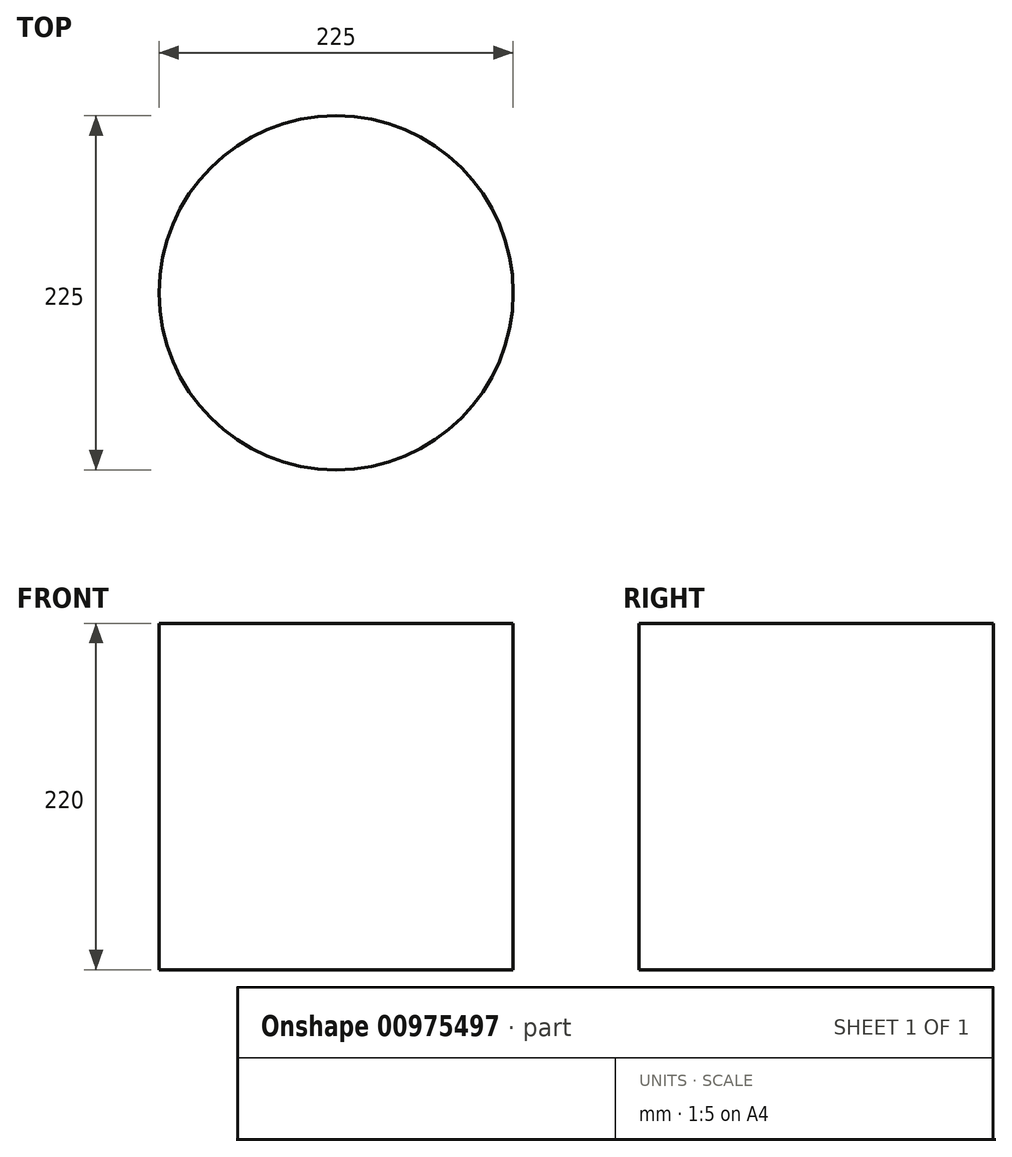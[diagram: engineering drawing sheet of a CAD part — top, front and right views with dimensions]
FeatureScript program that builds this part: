
annotation { "Feature Type Name" : "Feature", "Feature Type Description" : "" }
export const myFeature = defineFeature(function(context is Context, id is Id, definition is map)
    precondition{}
    {
        {
            var Q0;
            Q0=qCreatedBy(makeId("Top.planeOp"),FACE);
            var sketch = newSketch(context, id + "F0", { "sketchPlane" : qUnion([Q0])});
            skCircle(sketch, "E0", {"center": v(0, 0) * mm, "radius": 110.5 * mm});
            skSolve(sketch);
        }
        {
            var Q0;
            Q0=makeQuery(id+"FZp1IOzvvAJlaml_0.opExtrude","CAP_FACE",FACE,{"disambiguationData":[OSD([sQuery(id+"F0.wireOp",EDGE,"E0"),sQuery(id+"F0.wireOp",EDGE,"23mLYnDv-4DGy-9HvD-HQY2-InyFFMG0Vyq0")])],"isStart":false});
            var sketch = newSketch(context, id + "F1", { "sketchPlane" : qUnion([Q0])});
            skCircle(sketch, "E1", {"center": v(0, 0) * mm, "radius": 110 * mm});
            skSolve(sketch);
        }
        {
            var Q0;
            Q0=qCreatedBy(makeId("Top.planeOp"),FACE);
            var sketch = newSketch(context, id + "F2", { "sketchPlane" : qUnion([Q0])});
            skCircle(sketch, "E2", {"center": v(0, 0) * mm, "radius": 112.5 * mm});
            skSolve(sketch);
        }
        {
            var Q0;
            Q0 = qSketchRegion(id + "F2", true);
            extrude(context, id + "F3", {"entities" : qUnion([Q0]), "depth" : 220 * mm, "offsetDistance" : 25 * mm});
        }
    });
